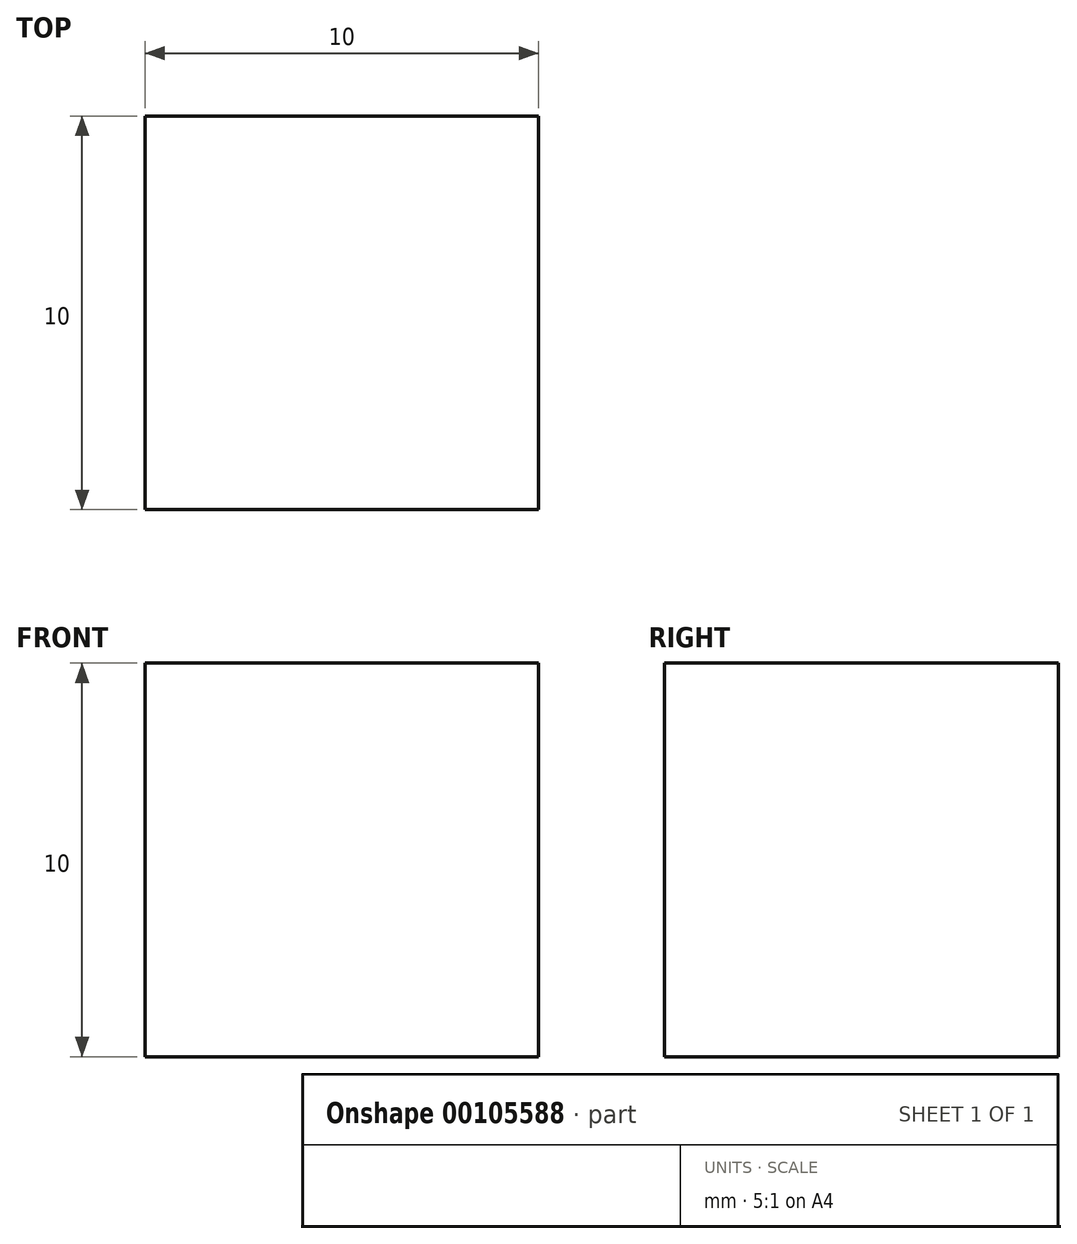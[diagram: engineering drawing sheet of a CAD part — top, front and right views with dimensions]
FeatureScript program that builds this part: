
annotation { "Feature Type Name" : "Feature", "Feature Type Description" : "" }
export const myFeature = defineFeature(function(context is Context, id is Id, definition is map)
    precondition{}
    {
        {
            var Q0;
            Q0=qCreatedBy(makeId("Top.planeOp"),FACE);
            var sketch = newSketch(context, id + "F0", { "sketchPlane" : qUnion([Q0])});
            skLineSegment(sketch, "E0.bottom", {"start": v(5, -5) * mm, "end": v(-5, -5) * mm});
            skLineSegment(sketch, "E0.top", {"start": v(5, 5) * mm, "end": v(-5, 5) * mm});
            skLineSegment(sketch, "E0.left", {"start": v(5, -5) * mm, "end": v(5, 5) * mm});
            skLineSegment(sketch, "E0.right", {"start": v(-5, -5) * mm, "end": v(-5, 5) * mm});
            skPoint(sketch, "E0.middle", {"position": v(0, 0) * mm});
            skSolve(sketch);
        }
        {
            var Q0;
            Q0 = qSketchRegion(id + "F0", true);
            extrude(context, id + "F1", {"entities" : qUnion([Q0]), "depth" : 10 * mm});
        }
    });
